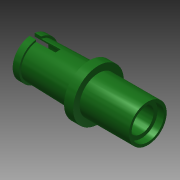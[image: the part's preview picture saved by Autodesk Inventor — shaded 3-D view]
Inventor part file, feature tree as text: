
AUTODESK INVENTOR PART (.ipt)
format: ipt  version: 2015 (Build 190159000, 159)  size: 158,720 bytes
history: native  units: in
note: dims shown in document units (in); Inventor stores cm internally (conversion verified against a paired STEP export)
features: sketch x2, revolve x1, extrude x1
ambient origin geometry x8: Origin, YZ Plane, XZ Plane, XY Plane, X Axis, Y Axis, Z Axis, Center Point
bodies: Solid1 (feature_tree)
feature tree (4):
  revolve  "Revolution1"  [1 undecoded]
  extrude  "Extrusion1"  Depth=0.04in
  sketch  "Sketch1"  dims[d0=0.33in d2=0.02in]
  sketch  "Sketch4"  dims[d3=0.03in d4=0.05in d5=0.07in d6=0.095in d7=0.01in d8=0.05in d9=0.05in d10=0.05in d11=0.19in d12=0.25in d13=0.025in d15=0.03in d16=90.0deg d18=0.04in d19=0.02in d21=0.0in d22=1.0in d23=0.2in d24=0.0in]
note: 1 required parameter value undecoded (feature->parameter linkage not recoverable at this tier; creation-order binding heuristic only, values carry confidence <= 0.55)
